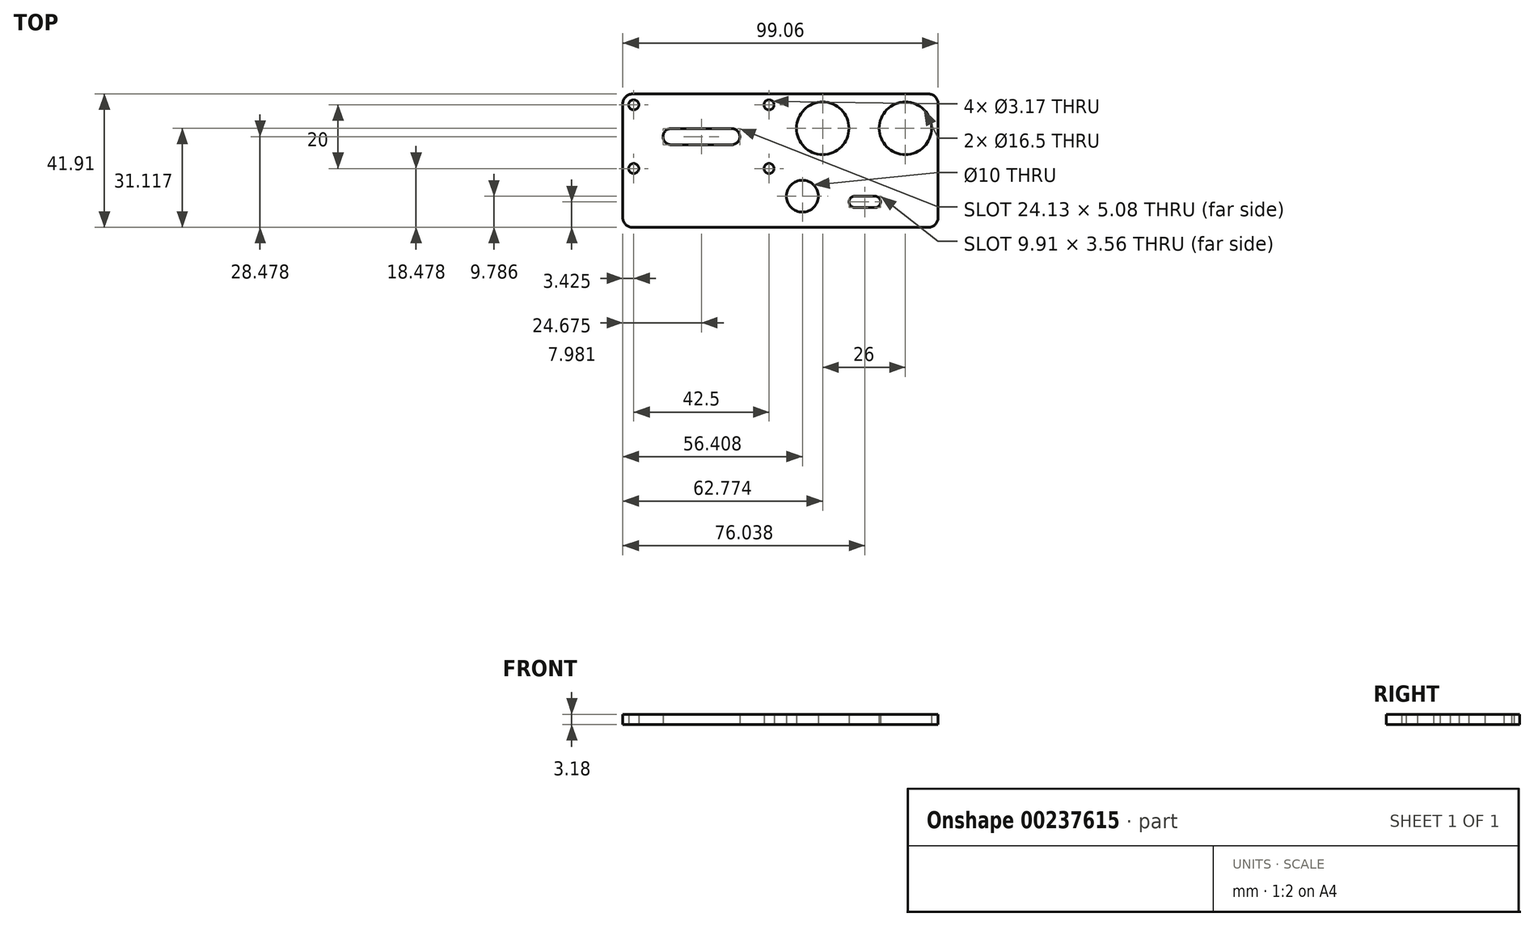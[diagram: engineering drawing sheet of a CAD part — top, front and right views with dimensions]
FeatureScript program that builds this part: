
annotation { "Feature Type Name" : "Feature", "Feature Type Description" : "" }
export const myFeature = defineFeature(function(context is Context, id is Id, definition is map)
    precondition{}
    {
        {
            var Q0;
            Q0=qCreatedBy(makeId("Top.planeOp"),FACE);
            var sketch = newSketch(context, id + "F0", { "sketchPlane" : qUnion([Q0])});
            skLineSegment(sketch, "E0.bottom", {"start": v(-49.22, 21.9) * mm, "end": v(49.84, 21.9) * mm});
            skLineSegment(sketch, "E0.top", {"start": v(-49.22, -20.01) * mm, "end": v(49.84, -20.01) * mm});
            skLineSegment(sketch, "E0.left", {"start": v(-49.22, 21.9) * mm, "end": v(-49.22, -20.01) * mm});
            skLineSegment(sketch, "E0.right", {"start": v(49.84, 21.9) * mm, "end": v(49.84, -20.01) * mm});
            skCircle(sketch, "E1", {"center": v(-45.8, 18.47) * mm, "radius": 1.59 * mm});
            skCircle(sketch, "E2", {"center": v(-45.8, -1.53) * mm, "radius": 1.59 * mm});
            skCircle(sketch, "E3", {"center": v(-3.3, -1.53) * mm, "radius": 1.59 * mm});
            skCircle(sketch, "E4", {"center": v(-3.3, 18.47) * mm, "radius": 1.59 * mm});
            skLineSegment(sketch, "E5.bottom", {"start": v(-3.3, -1.53) * mm, "end": v(-45.8, -1.53) * mm, "construction": true});
            skLineSegment(sketch, "E5.top", {"start": v(-3.3, 18.47) * mm, "end": v(-45.8, 18.47) * mm, "construction": true});
            skLineSegment(sketch, "E5.left", {"start": v(-3.3, -1.53) * mm, "end": v(-3.3, 18.47) * mm, "construction": true});
            skLineSegment(sketch, "E5.right", {"start": v(-45.8, -1.53) * mm, "end": v(-45.8, 18.47) * mm, "construction": true});
            skPoint(sketch, "E5.middle", {"position": v(-24.54, 8.47) * mm});
            skCircle(sketch, "E6", {"center": v(13.55, 11.1) * mm, "radius": 8.25 * mm});
            skCircle(sketch, "E7", {"center": v(39.55, 11.1) * mm, "radius": 8.25 * mm});
            skLineSegment(sketch, "E8", {"start": v(13.55, 11.1) * mm, "end": v(39.55, 11.1) * mm, "construction": true});
            skLineSegment(sketch, "E9", {"start": v(-34.07, 8.47) * mm, "end": v(-15.02, 8.47) * mm, "construction": true});
            skArc(sketch, "E10.0.startCap", {"start": v(-34.07, 5.93) * mm, "mid": v(-36.6, 8.47) * mm, "end": v(-34.07, 11) * mm});
            skArc(sketch, "E10.0.endCap", {"start": v(-15.02, 11) * mm, "mid": v(-12.48, 8.47) * mm, "end": v(-15.02, 5.93) * mm});
            skLineSegment(sketch, "E10.0.left", {"start": v(-34.07, 11) * mm, "end": v(-15.02, 11) * mm});
            skLineSegment(sketch, "E10.0.right", {"start": v(-34.07, 5.93) * mm, "end": v(-15.02, 5.93) * mm});
            skLineSegment(sketch, "E11", {"start": v(-45.8, 18.47) * mm, "end": v(-49.22, 18.47) * mm, "construction": true});
            skLineSegment(sketch, "E12", {"start": v(-45.8, 18.47) * mm, "end": v(-45.8, 21.9) * mm, "construction": true});
            skCircle(sketch, "E13", {"center": v(7.19, -10.22) * mm, "radius": 5 * mm});
            skLineSegment(sketch, "E14", {"start": v(23.64, -12.03) * mm, "end": v(30, -12.03) * mm, "construction": true});
            skArc(sketch, "E15.0.startCap", {"start": v(23.64, -13.8) * mm, "mid": v(21.86, -12.03) * mm, "end": v(23.64, -10.25) * mm});
            skArc(sketch, "E15.0.endCap", {"start": v(30, -10.25) * mm, "mid": v(31.77, -12.03) * mm, "end": v(30, -13.8) * mm});
            skLineSegment(sketch, "E15.0.left", {"start": v(23.64, -10.25) * mm, "end": v(30, -10.25) * mm});
            skLineSegment(sketch, "E15.0.right", {"start": v(23.64, -13.8) * mm, "end": v(30, -13.8) * mm});
            skSolve(sketch);
        }
        {
            var Q0;
            Q0=makeQuery(id+"F0.imprint","IMPRINT",FACE,{"disambiguationData":[TD([[makeQuery(id+"F0.imprint","IMPRINT",EDGE,{"derivedFrom":sQuery(id+"F0.wireOp",EDGE,"E0.bottom")}),-1.0]])]});
            extrude(context, id + "F1", {"entities" : qUnion([Q0]), "depth" : 3.17 * mm});
        }
        {
            var Q0;
            Q0=makeQuery(id+"F1.opExtrude","SWEPT_EDGE",EDGE,{"disambiguationData":[OSD([sQuery(id+"F0.wireOp",EDGE,"E0.bottom"),sQuery(id+"F0.wireOp",EDGE,"E0.right")])]});
            var Q1;
            Q1=makeQuery(id+"F1.opExtrude","SWEPT_EDGE",EDGE,{"disambiguationData":[OSD([sQuery(id+"F0.wireOp",EDGE,"E0.top"),sQuery(id+"F0.wireOp",EDGE,"E0.right")])]});
            var Q2;
            Q2=makeQuery(id+"F1.opExtrude","SWEPT_EDGE",EDGE,{"disambiguationData":[OSD([sQuery(id+"F0.wireOp",EDGE,"E0.top"),sQuery(id+"F0.wireOp",EDGE,"E0.left")])]});
            var Q3;
            Q3=makeQuery(id+"F1.opExtrude","SWEPT_EDGE",EDGE,{"disambiguationData":[OSD([sQuery(id+"F0.wireOp",EDGE,"E0.bottom"),sQuery(id+"F0.wireOp",EDGE,"E0.left")])]});
            fillet(context, id + "F2", {"entities" : qUnion([Q0, Q1, Q2, Q3]), "radius" : 3.05 * mm, "tangentPropagation" : true, "allowEdgeOverflow" : false});
        }
    });
